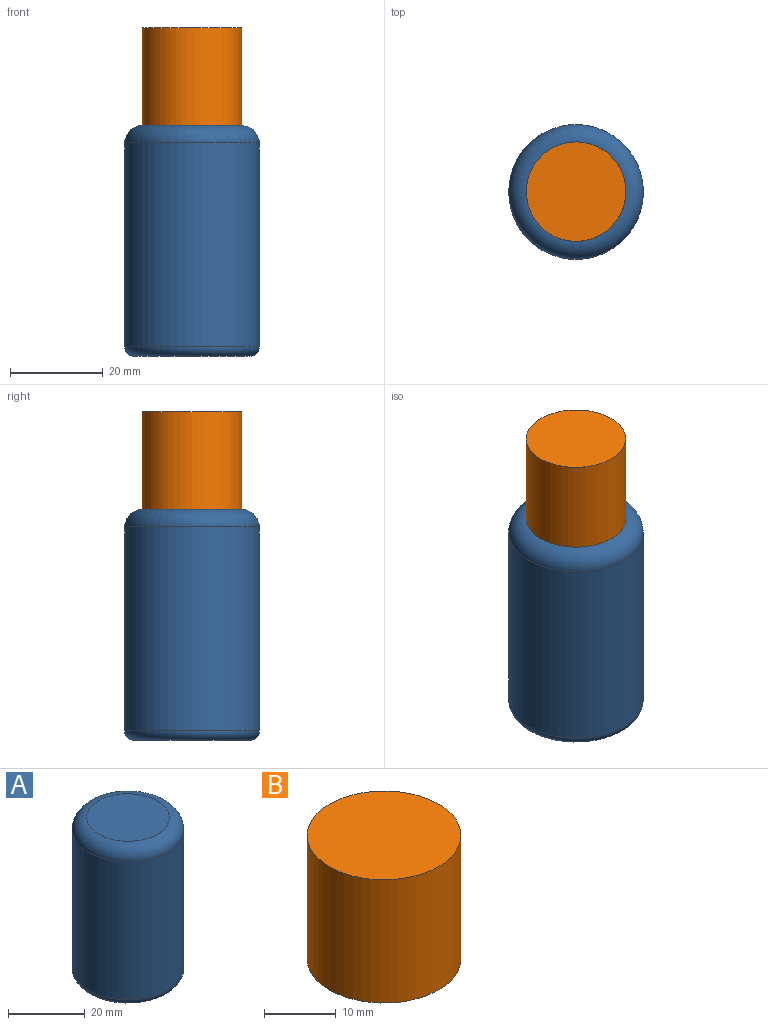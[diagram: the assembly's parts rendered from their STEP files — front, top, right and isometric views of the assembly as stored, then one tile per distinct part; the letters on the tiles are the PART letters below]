
ASSEMBLY  parts=2 mates=1
PART A: 5 faces, bbox 31.5x31.5x49.9 mm
  f0: plane 25.1x25.1mm, normal (0,0,-1), area 494.8mm2, adj f4
  f1: plane 21.5x21.5mm, normal (0,0,1), area 363.1mm2, adj f2
  f2: torus R=10.75mm, axis (0,0,-1), area 493.9mm2, adj f1,f3
  f3: cylinder r=14.55mm len=44.1mm, axis (0,0,-1), area 4031.6mm2, adj f2,f4
  f4: torus R=12.55mm, axis (0,0,-1), area 272.9mm2, adj f0,f3
PART B: 3 faces, bbox 21.5x21.5x21.1 mm
  f0: cylinder r=10.75mm len=21.5mm, axis (0,0,-1), area 1425.2mm2, adj f1,f2
  f1: plane 21.5x21.5mm, normal (0,0,1), area 363.1mm2, adj f0
  f2: plane 21.5x21.5mm, normal (0,0,-1), area 363.1mm2, adj f0
PLACE A t=(-32.45,-15.14,5.39)mm
PLACE B t=(-32.45,-15.14,5.39)mm
MATE fastened A.f2 <-> B.f0  axis (0,0,1) through (-32.45,-15.14,55.29)mm
